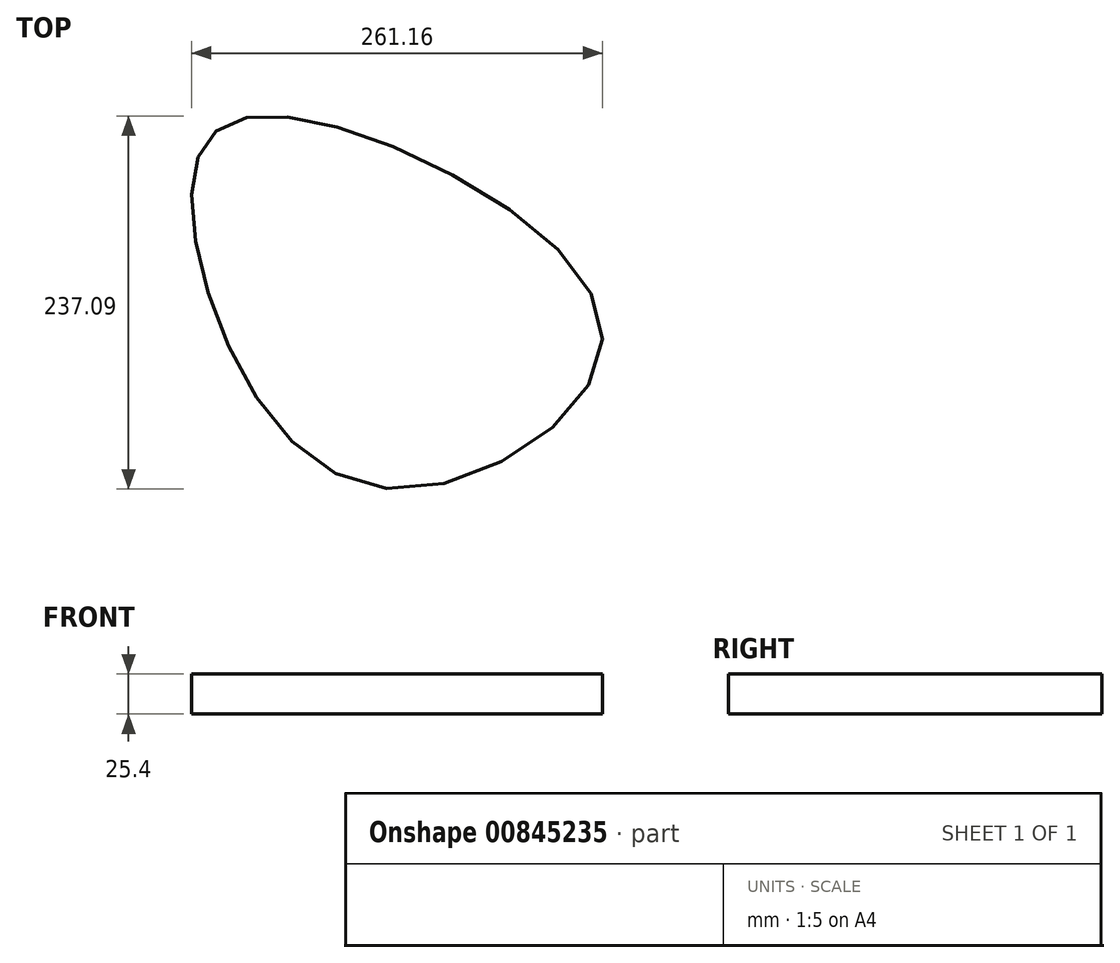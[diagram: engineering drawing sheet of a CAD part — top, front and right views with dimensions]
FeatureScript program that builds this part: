
annotation { "Feature Type Name" : "Feature", "Feature Type Description" : "" }
export const myFeature = defineFeature(function(context is Context, id is Id, definition is map)
    precondition{}
    {
        {
            var Q0;
            Q0=qCreatedBy(makeId("Top.planeOp"),FACE);
            var sketch = newSketch(context, id + "F0", { "sketchPlane" : qUnion([Q0])});
            skFitSpline(sketch, "E0", {"points": [v(-111.82, 32.74) * mm, v(-109.06, 133.17) * mm, v(0, 127.47) * mm, v(138.6, 0) * mm, v(0, -91.74) * mm, v(-111.82, 32.74) * mm]});
            skSolve(sketch);
        }
        {
            var Q0;
            Q0=makeQuery(id+"F0.imprint","IMPRINT",FACE,{"disambiguationData":[TD([[makeQuery(id+"F0.imprint","IMPRINT",EDGE,{"derivedFrom":sQuery(id+"F0.wireOp",EDGE,"E0")}),-1.0]])]});
            extrude(context, id + "F1", {"entities" : qUnion([Q0]), "depth" : 25.4 * mm, "offsetDistance" : 25.4 * mm});
        }
    });
